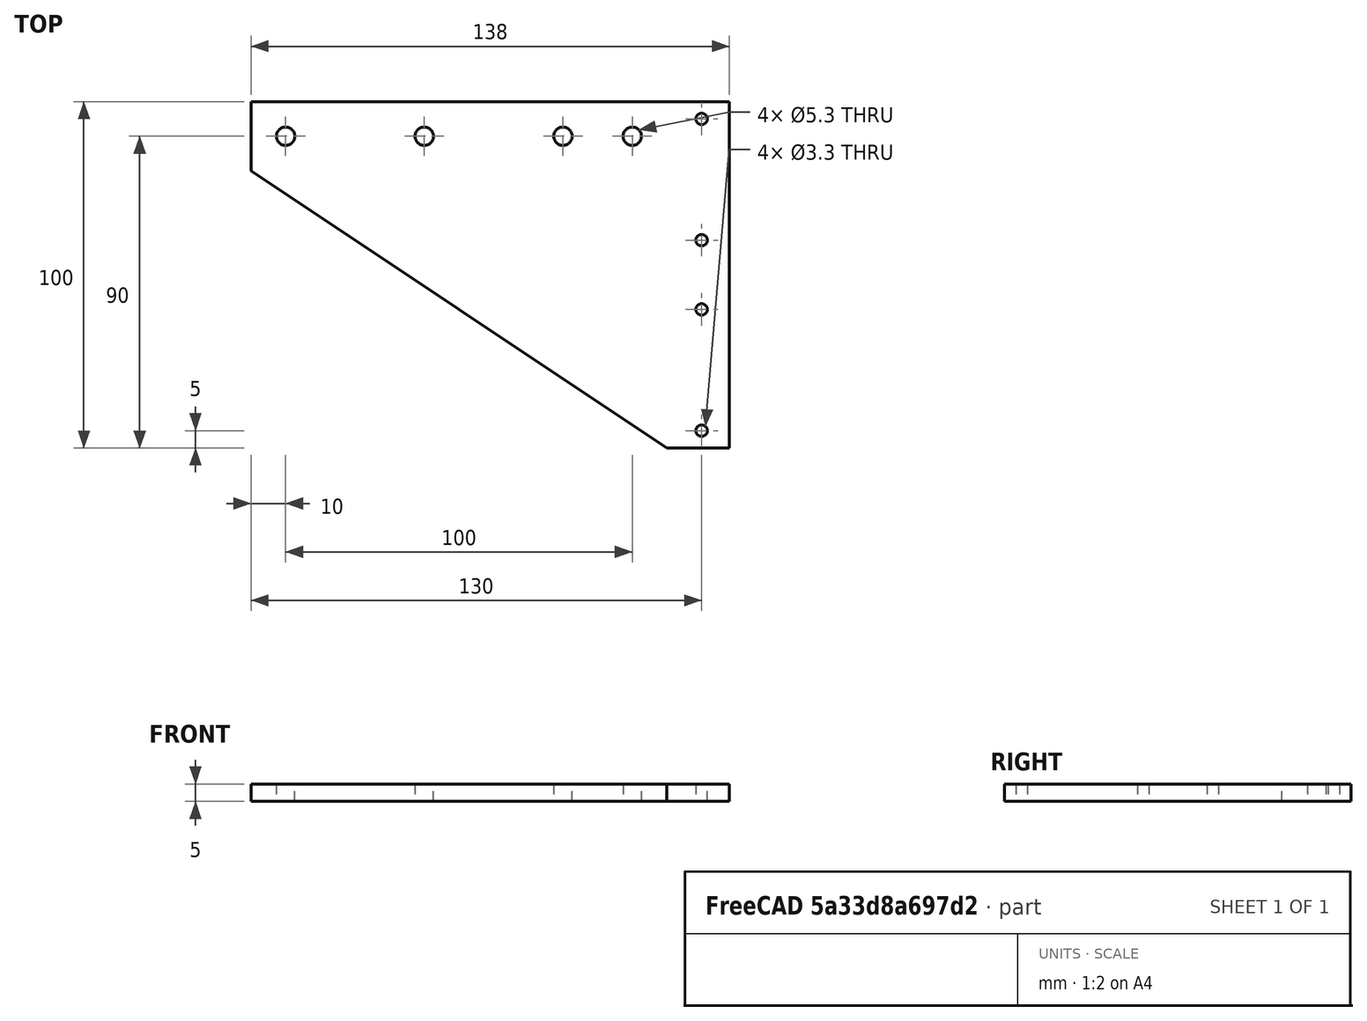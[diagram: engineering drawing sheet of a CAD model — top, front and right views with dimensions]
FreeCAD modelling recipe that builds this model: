
FCSTD DOCUMENT  (FreeCAD 0.19R20209 (Git))
Label: Z-Axel-Bearing_031c2
License: Creative Commons Attribution
LicenseURL: http://creativecommons.org/licenses/by/4.0/
objects: Sketcher::SketchObject×1, PartDesign::Pad×1, PartDesign::Body×1
note: 4 computed .brp shape members not serialized (recipe doc carries the construction recipe); baked Part::Feature solids carry a one-line shape summary decoded from their .brp

FEATURE [Sketcher::SketchObject] Sketch
  MapMode = 5
  Support = -> [XY_Plane]
  expr: Constraints[10] = 100 + 20 + 18
  sketch-geometry (13):
    g0: LineSegment StartX=-120 StartY=20 StartZ=0 EndX=18 EndY=20 EndZ=0
    g1: LineSegment StartX=18 StartY=20 StartZ=0 EndX=18 EndY=-80 EndZ=0
    g2: LineSegment StartX=18 StartY=-80 StartZ=0 EndX=0 EndY=-80 EndZ=0
    g3: LineSegment StartX=0 StartY=-80 StartZ=0 EndX=-120 EndY=0 EndZ=0
    g4: LineSegment StartX=-120 StartY=0 StartZ=0 EndX=-120 EndY=20 EndZ=0
    g5: Circle CenterX=-10 CenterY=10 CenterZ=0 NormalX=0 NormalY=0 NormalZ=1 AngleXU=0 Radius=2.65
    g6: Circle CenterX=-110 CenterY=10 CenterZ=0 NormalX=0 NormalY=0 NormalZ=1 AngleXU=0 Radius=2.65
    g7: Circle CenterX=-70 CenterY=10 CenterZ=0 NormalX=0 NormalY=0 NormalZ=1 AngleXU=0 Radius=2.65
    g8: Circle CenterX=-30 CenterY=10 CenterZ=0 NormalX=0 NormalY=0 NormalZ=1 AngleXU=0 Radius=2.65
    g9: Circle CenterX=10 CenterY=15 CenterZ=0 NormalX=0 NormalY=0 NormalZ=1 AngleXU=0 Radius=1.65
    g10: Circle CenterX=10 CenterY=-20 CenterZ=0 NormalX=0 NormalY=0 NormalZ=1 AngleXU=0 Radius=1.65
    g11: Circle CenterX=10 CenterY=-40 CenterZ=0 NormalX=0 NormalY=0 NormalZ=1 AngleXU=0 Radius=1.65
    g12: Circle CenterX=10 CenterY=-75 CenterZ=0 NormalX=0 NormalY=0 NormalZ=1 AngleXU=0 Radius=1.65
  constraints (38):
    c: Horizontal(g0)
    c: Vertical(g1)
    c: Coincident(g1,g2)
    c: Horizontal(g2)
    c: Coincident(g2,g3)
    c: Coincident(g3,g4)
    c: Vertical(g4)
    c: Coincident(g4,g0)
    c: PointOnObject(g3,g-1)
    c: DistanceY(g4,g4) = 20
    c: DistanceX(g0,g1) = 138
    c: DistanceX(g2,g2) = 18
    c: PointOnObject(g2,g-2)
    c: DistanceY(g1,g1) = 100
    c: Coincident(g0,g1)
    c: Diameter(g5) = 5.3
    c: DistanceY(g-1,g5) = 10
    c: DistanceX(g5,g-1) = 10
    c: Horizontal(g6,g7)
    c: Horizontal(g8,g5)
    c: Symmetric(g6,g8,g7)
    c: DistanceX(g6,g8) = 80
    c: DistanceX(g3,g6) = 10
    c: Equal(g8,g5)
    c: Equal(g6,g7)
    c: Equal(g7,g8)
    c: Equal(g12,g11)
    c: Equal(g11,g10)
    c: Equal(g10,g9)
    c: Diameter(g9) = 3.3
    c: Vertical(g12,g11)
    c: Vertical(g11,g10)
    c: Vertical(g10,g9)
    c: DistanceY(g12,g9) = 90
    c: DistanceX(g5,g9) = 20
    c: DistanceY(g10,g9) = 35
    c: DistanceY(g11,g10) = 20
    c: DistanceY(g9,g0) = 5
FEATURE [PartDesign::Pad] Pad
  Length = 5
  Length2 = 100
  Profile = -> Sketch
  Refine = true
  Type = 0
FEATURE [PartDesign::Body] Body
  Group = -> [Sketch,Pad]
  Origin = -> Origin
  Tip = -> Pad
